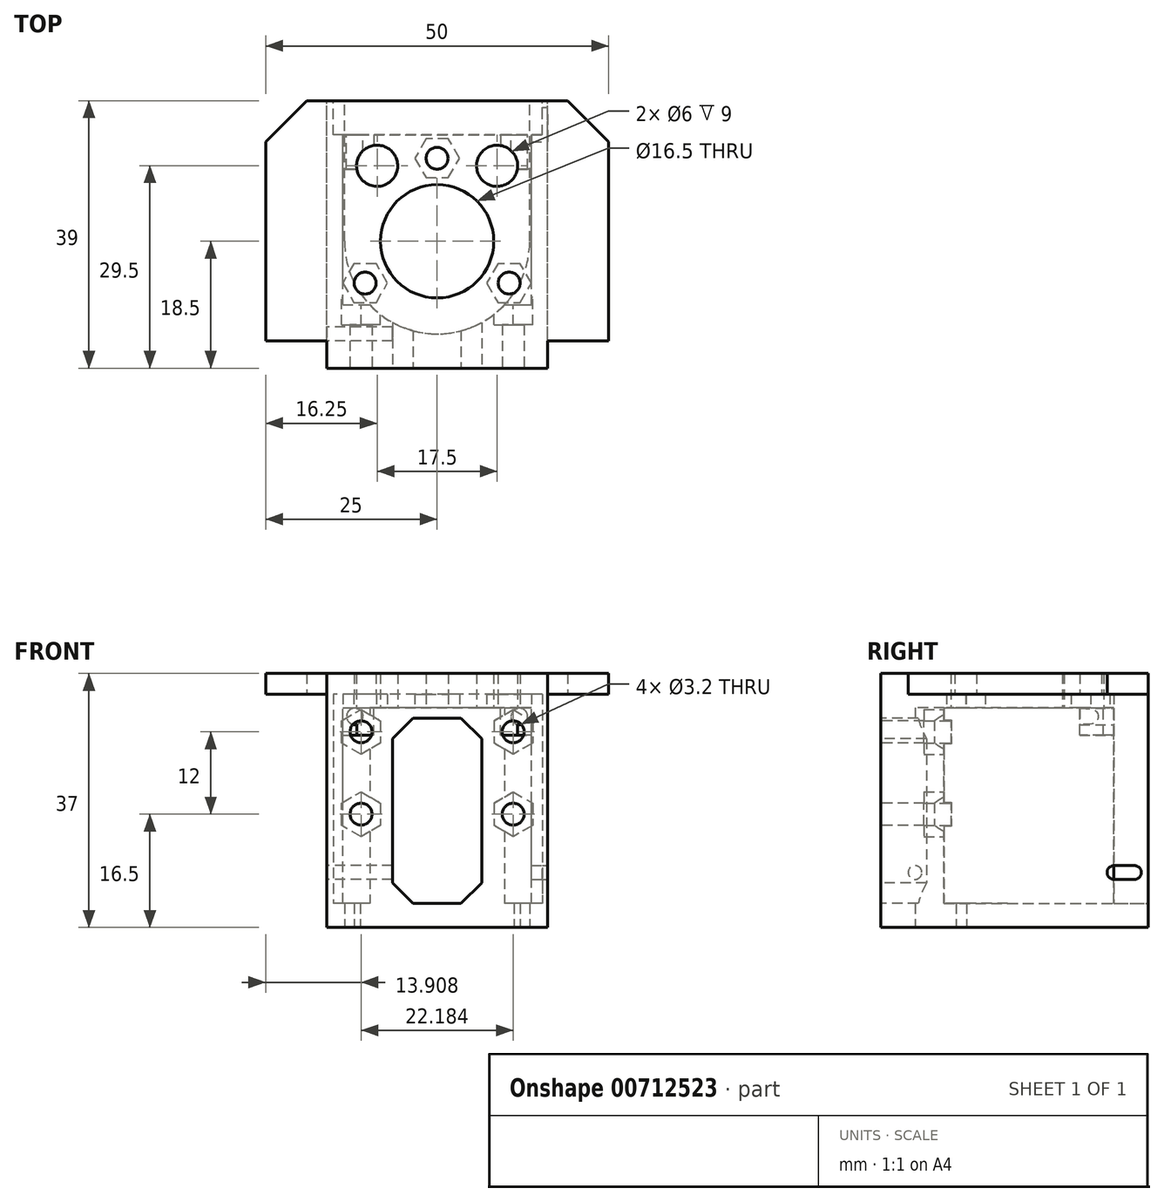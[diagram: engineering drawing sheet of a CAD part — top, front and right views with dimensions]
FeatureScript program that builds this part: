
annotation { "Feature Type Name" : "Feature", "Feature Type Description" : "" }
export const myFeature = defineFeature(function(context is Context, id is Id, definition is map)
    precondition{}
    {
        {
            var Q0;
            Q0=qCreatedBy(makeId("Top.planeOp"),FACE);
            var sketch = newSketch(context, id + "F0", { "sketchPlane" : qUnion([Q0])});
            skLineSegment(sketch, "E0", {"start": v(-25, 0) * mm, "end": v(-25, 29) * mm});
            skLineSegment(sketch, "E1", {"start": v(-25, 29) * mm, "end": v(-19, 35) * mm});
            skLineSegment(sketch, "E2", {"start": v(-19, 35) * mm, "end": v(19, 35) * mm});
            skLineSegment(sketch, "E3", {"start": v(19, 35) * mm, "end": v(25, 29) * mm});
            skLineSegment(sketch, "E4", {"start": v(25, 29) * mm, "end": v(25, 0) * mm});
            skLineSegment(sketch, "E5", {"start": v(25, 0) * mm, "end": v(16.1, 0) * mm});
            skLineSegment(sketch, "E6", {"start": v(16.1, 0) * mm, "end": v(16.1, -4) * mm});
            skLineSegment(sketch, "E7", {"start": v(16.1, -4) * mm, "end": v(-16.1, -4) * mm});
            skLineSegment(sketch, "E8", {"start": v(-16.1, -4) * mm, "end": v(-16.1, 0) * mm});
            skLineSegment(sketch, "E9", {"start": v(-16.1, 0) * mm, "end": v(-25, 0) * mm});
            skCircle(sketch, "E10", {"center": v(0, 14.5) * mm, "radius": 8.25 * mm});
            skCircle(sketch, "E11", {"center": v(0, 26.6) * mm, "radius": 1.6 * mm});
            skCircle(sketch, "E12", {"center": v(-10.5, 8.4) * mm, "radius": 1.6 * mm});
            skCircle(sketch, "E13", {"center": v(10.5, 8.4) * mm, "radius": 1.6 * mm});
            skCircle(sketch, "E14", {"center": v(-8.75, 25.5) * mm, "radius": 3 * mm});
            skCircle(sketch, "E15", {"center": v(8.75, 25.5) * mm, "radius": 3 * mm});
            skSolve(sketch);
        }
        {
            var Q0;
            Q0=makeQuery(id+"F0.imprint","IMPRINT",FACE,{"disambiguationData":[TD([[makeQuery(id+"F0.imprint","IMPRINT",EDGE,{"derivedFrom":sQuery(id+"F0.wireOp",EDGE,"E0")}),-1.0]])]});
            extrude(context, id + "F1", {"entities" : qUnion([Q0]), "depth" : 3 * mm, "offsetDistance" : 25 * mm});
        }
        {
            var Q0;
            Q0=makeQuery(id+"F1.opExtrude","CAP_FACE",FACE,{"disambiguationData":[OSD([sQuery(id+"F0.wireOp",EDGE,"E0"),sQuery(id+"F0.wireOp",EDGE,"E1"),sQuery(id+"F0.wireOp",EDGE,"E2"),sQuery(id+"F0.wireOp",EDGE,"E3"),sQuery(id+"F0.wireOp",EDGE,"E4"),sQuery(id+"F0.wireOp",EDGE,"E5"),sQuery(id+"F0.wireOp",EDGE,"E6"),sQuery(id+"F0.wireOp",EDGE,"E7"),sQuery(id+"F0.wireOp",EDGE,"E8"),sQuery(id+"F0.wireOp",EDGE,"E9"),sQuery(id+"F0.wireOp",EDGE,"E10"),sQuery(id+"F0.wireOp",EDGE,"E11"),sQuery(id+"F0.wireOp",EDGE,"E12"),sQuery(id+"F0.wireOp",EDGE,"E13"),sQuery(id+"F0.wireOp",EDGE,"E14"),sQuery(id+"F0.wireOp",EDGE,"E15")])],"isStart":true});
            var sketch = newSketch(context, id + "F2", { "sketchPlane" : qUnion([Q0])});
            skLineSegment(sketch, "E16.bottom", {"start": v(-16.1, 4) * mm, "end": v(16.1, 4) * mm});
            skLineSegment(sketch, "E16.top", {"start": v(-16.1, -35) * mm, "end": v(16.1, -35) * mm});
            skLineSegment(sketch, "E16.left", {"start": v(-16.1, 4) * mm, "end": v(-16.1, -35) * mm});
            skLineSegment(sketch, "E16.right", {"start": v(16.1, 4) * mm, "end": v(16.1, -35) * mm});
            skSolve(sketch);
        }
        {
            var Q0;
            {var subQ4=sQuery(id+"F2.wireOp",EDGE,"E16.bottom");Q0=makeQuery(id+"F2.imprint","IMPRINT",FACE,{"disambiguationData":[TD([[makeQuery(id+"F2.imprint","IMPRINT",EDGE,{"derivedFrom":subQ4}),1.0]])]});}
            extrude(context, id + "F3", {"entities" : qUnion([Q0]), "operationType" : NewBodyOperationType.ADD, "depth" : 34 * mm, "offsetDistance" : 25 * mm});
        }
        {
            var Q0;
            Q0=makeQuery(id+"F3.boolean.opBoolean","MERGE",FACE,{"derivedFrom":[makeQuery(id+"F1.opExtrude","SWEPT_FACE",FACE,{"disambiguationData":[OSD([sQuery(id+"F0.wireOp",EDGE,"E2")])]}),makeQuery(id+"F3.opExtrude","SWEPT_FACE",FACE,{"disambiguationData":[OSD([sQuery(id+"F2.wireOp",EDGE,"E16.top")])]})]});
            var sketch = newSketch(context, id + "F4", { "sketchPlane" : qUnion([Q0])});
            skLineSegment(sketch, "E17.bottom", {"start": v(-15.34, 0) * mm, "end": v(15.16, 0) * mm});
            skLineSegment(sketch, "E17.top", {"start": v(-15.34, -30.5) * mm, "end": v(15.16, -30.5) * mm});
            skLineSegment(sketch, "E17.left", {"start": v(-15.34, 0) * mm, "end": v(-15.34, -30.5) * mm});
            skLineSegment(sketch, "E17.right", {"start": v(15.16, 0) * mm, "end": v(15.16, -30.5) * mm});
            skSolve(sketch);
        }
        {
            var Q0;
            Q0=makeQuery(id+"F4.imprint","IMPRINT",FACE,{"disambiguationData":[TD([[makeQuery(id+"F4.imprint","IMPRINT",EDGE,{"derivedFrom":sQuery(id+"F4.wireOp",EDGE,"E17.bottom")}),-1.0]])]});
            extrude(context, id + "F5", {"entities" : qUnion([Q0]), "operationType" : NewBodyOperationType.REMOVE, "oppositeDirection" : true, "depth" : 5 * mm, "offsetDistance" : 25 * mm});
        }
        {
            var Q0;
            Q0=makeQuery(id+"F5.boolean.opBoolean","COPY",FACE,{"derivedFrom":makeQuery(id+"F5.opExtrude","CAP_FACE",FACE,{"disambiguationData":[OSD([sQuery(id+"F4.wireOp",EDGE,"E17.bottom"),sQuery(id+"F4.wireOp",EDGE,"E17.top"),sQuery(id+"F4.wireOp",EDGE,"E17.left"),sQuery(id+"F4.wireOp",EDGE,"E17.right")])],"isStart":false})});
            var sketch = newSketch(context, id + "F6", { "sketchPlane" : qUnion([Q0])});
            skLineSegment(sketch, "E18.bottom", {"start": v(13.75, -30.5) * mm, "end": v(-13.75, -30.5) * mm});
            skLineSegment(sketch, "E18.top", {"start": v(13.75, -2) * mm, "end": v(-13.75, -2) * mm});
            skLineSegment(sketch, "E18.left", {"start": v(13.75, -30.5) * mm, "end": v(13.75, -2) * mm});
            skLineSegment(sketch, "E18.right", {"start": v(-13.75, -30.5) * mm, "end": v(-13.75, -2) * mm});
            skPoint(sketch, "E18.middle", {"position": v(0, -16.25) * mm});
            skSolve(sketch);
        }
        {
            var Q0;
            Q0=makeQuery(id+"F6.imprint","IMPRINT",FACE,{"disambiguationData":[TD([[makeQuery(id+"F6.imprint","IMPRINT",EDGE,{"derivedFrom":sQuery(id+"F6.wireOp",EDGE,"E18.bottom")}),1.0]])]});
            extrude(context, id + "F7", {"entities" : qUnion([Q0]), "operationType" : NewBodyOperationType.REMOVE, "oppositeDirection" : true, "depth" : 24.77 * mm, "offsetDistance" : 25 * mm});
        }
        {
            var Q0;
            Q0=makeQuery(id+"F3.opExtrude","CAP_FACE",FACE,{"disambiguationData":[OSD([sQuery(id+"F0.wireOp",EDGE,"E10"),sQuery(id+"F0.wireOp",EDGE,"E11"),sQuery(id+"F0.wireOp",EDGE,"E12"),sQuery(id+"F0.wireOp",EDGE,"E13"),sQuery(id+"F0.wireOp",EDGE,"E14"),sQuery(id+"F0.wireOp",EDGE,"E15"),sQuery(id+"F2.wireOp",EDGE,"E16.bottom"),sQuery(id+"F2.wireOp",EDGE,"E16.top"),sQuery(id+"F2.wireOp",EDGE,"E16.left"),sQuery(id+"F2.wireOp",EDGE,"E16.right")])],"isStart":false});
            var sketch = newSketch(context, id + "F8", { "sketchPlane" : qUnion([Q0])});
            skCircle(sketch, "E19", {"center": v(0, -14.5) * mm, "radius": 13.5 * mm});
            skLineSegment(sketch, "E20.bottom", {"start": v(13.5, -14.5) * mm, "end": v(-13.5, -14.5) * mm});
            skLineSegment(sketch, "E20.top", {"start": v(13.5, -55.5) * mm, "end": v(-13.5, -55.5) * mm});
            skLineSegment(sketch, "E20.left", {"start": v(13.5, -14.5) * mm, "end": v(13.5, -55.5) * mm});
            skLineSegment(sketch, "E20.right", {"start": v(-13.5, -14.5) * mm, "end": v(-13.5, -55.5) * mm});
            skPoint(sketch, "E20.middle", {"position": v(0, -35) * mm});
            skSolve(sketch);
        }
        {
            var Q0;
            {var subQ2=sQuery(id+"F8.wireOp",EDGE,"E19");var subQ9=makeQuery(id+"F3.opExtrude","CAP_EDGE",EDGE,{"disambiguationData":[OSD([sQuery(id+"F0.wireOp",EDGE,"E14")])],"isStart":false});var subQ10=makeQuery(id+"F8.imprint","INTERSECT",VERTEX,{"disambiguationData":[OD(1.0)],"derivedFrom":[subQ9,subQ2]});Q0=makeQuery(id+"F8.imprint","IMPRINT",FACE,{"disambiguationData":[TD([[makeQuery(id+"F8.imprint","IMPRINT",EDGE,{"disambiguationData":[TD([[subQ10,-1.0]])],"derivedFrom":subQ2}),-1.0]])]});}
            var Q1;
            {var subQ1=sQuery(id+"F8.wireOp",EDGE,"E19");var subQ8=makeQuery(id+"F3.opExtrude","CAP_EDGE",EDGE,{"disambiguationData":[OSD([sQuery(id+"F0.wireOp",EDGE,"E14")])],"isStart":false});var subQ9=makeQuery(id+"F8.imprint","INTERSECT",VERTEX,{"disambiguationData":[OD(1.0)],"derivedFrom":[subQ8,subQ1]});Q1=makeQuery(id+"F8.imprint","IMPRINT",FACE,{"disambiguationData":[TD([[makeQuery(id+"F8.imprint","IMPRINT",EDGE,{"disambiguationData":[TD([[subQ9,-1.0]])],"derivedFrom":subQ1}),1.0]])]});}
            var Q2;
            {var subQ1=sQuery(id+"F8.wireOp",EDGE,"E19");var subQ9=makeQuery(id+"F3.opExtrude","CAP_EDGE",EDGE,{"disambiguationData":[OSD([sQuery(id+"F0.wireOp",EDGE,"E13")])],"isStart":false});var subQ10=makeQuery(id+"F8.imprint","INTERSECT",VERTEX,{"disambiguationData":[OD(1.0)],"derivedFrom":[subQ9,subQ1]});Q2=makeQuery(id+"F8.imprint","IMPRINT",FACE,{"disambiguationData":[TD([[makeQuery(id+"F8.imprint","IMPRINT",EDGE,{"disambiguationData":[TD([[subQ10,-1.0]])],"derivedFrom":subQ1}),1.0]])]});}
            extrude(context, id + "F9", {"entities" : qUnion([Q0, Q1, Q2]), "operationType" : NewBodyOperationType.REMOVE, "oppositeDirection" : true, "depth" : 32 * mm, "offsetDistance" : 25 * mm});
        }
        {
            var Q0;
            Q0=makeQuery(id+"F3.boolean.opBoolean","MERGE",FACE,{"derivedFrom":[makeQuery(id+"F1.opExtrude","SWEPT_FACE",FACE,{"disambiguationData":[OSD([sQuery(id+"F0.wireOp",EDGE,"E7")])]}),makeQuery(id+"F3.opExtrude","SWEPT_FACE",FACE,{"disambiguationData":[OSD([sQuery(id+"F2.wireOp",EDGE,"E16.bottom")])]})]});
            var sketch = newSketch(context, id + "F10", { "sketchPlane" : qUnion([Q0])});
            skLineSegment(sketch, "E21", {"start": v(-6.5, -6.5) * mm, "end": v(-6.5, -27.5) * mm});
            skLineSegment(sketch, "E22", {"start": v(-6.5, -27.5) * mm, "end": v(-3.5, -30.5) * mm});
            skLineSegment(sketch, "E23", {"start": v(-3.5, -30.5) * mm, "end": v(3.5, -30.5) * mm});
            skLineSegment(sketch, "E24", {"start": v(3.5, -30.5) * mm, "end": v(6.5, -27.5) * mm});
            skLineSegment(sketch, "E25", {"start": v(6.5, -27.5) * mm, "end": v(6.5, -6.5) * mm});
            skLineSegment(sketch, "E26", {"start": v(6.5, -6.5) * mm, "end": v(3.5, -3.5) * mm});
            skLineSegment(sketch, "E27", {"start": v(3.5, -3.5) * mm, "end": v(-3.5, -3.5) * mm});
            skLineSegment(sketch, "E28", {"start": v(-3.5, -3.5) * mm, "end": v(-6.5, -6.5) * mm});
            skCircle(sketch, "E29", {"center": v(-11.1, -5.5) * mm, "radius": 1.6 * mm});
            skCircle(sketch, "E30", {"center": v(-11.1, -17.5) * mm, "radius": 1.6 * mm});
            skCircle(sketch, "E31", {"center": v(11.1, -5.5) * mm, "radius": 1.6 * mm});
            skCircle(sketch, "E32", {"center": v(11.1, -17.5) * mm, "radius": 1.6 * mm});
            skSolve(sketch);
        }
        {
            var Q0;
            Q0=makeQuery(id+"F10.imprint","IMPRINT",FACE,{"disambiguationData":[TD([[makeQuery(id+"F10.imprint","IMPRINT",EDGE,{"derivedFrom":sQuery(id+"F10.wireOp",EDGE,"E29")}),1.0]])]});
            var Q1;
            Q1=makeQuery(id+"F10.imprint","IMPRINT",FACE,{"disambiguationData":[TD([[makeQuery(id+"F10.imprint","IMPRINT",EDGE,{"derivedFrom":sQuery(id+"F10.wireOp",EDGE,"E21")}),1.0]])]});
            var Q2;
            Q2=makeQuery(id+"F10.imprint","IMPRINT",FACE,{"disambiguationData":[TD([[makeQuery(id+"F10.imprint","IMPRINT",EDGE,{"derivedFrom":sQuery(id+"F10.wireOp",EDGE,"E30")}),1.0]])]});
            var Q3;
            Q3=makeQuery(id+"F10.imprint","IMPRINT",FACE,{"disambiguationData":[TD([[makeQuery(id+"F10.imprint","IMPRINT",EDGE,{"derivedFrom":sQuery(id+"F10.wireOp",EDGE,"E32")}),1.0]])]});
            var Q4;
            Q4=makeQuery(id+"F10.imprint","IMPRINT",FACE,{"disambiguationData":[TD([[makeQuery(id+"F10.imprint","IMPRINT",EDGE,{"derivedFrom":sQuery(id+"F10.wireOp",EDGE,"E31")}),1.0]])]});
            extrude(context, id + "F11", {"entities" : qUnion([Q0, Q1, Q2, Q3, Q4]), "operationType" : NewBodyOperationType.REMOVE, "endBound" : BoundingType.THROUGH_ALL, "oppositeDirection" : true, "depth" : 25 * mm, "offsetDistance" : 25 * mm});
        }
        {
            var Q0;
            Q0=makeQuery(id+"F9.boolean.opBoolean","MERGE",FACE,{"derivedFrom":[makeQuery(id+"F7.boolean.opBoolean","COPY",FACE,{"derivedFrom":makeQuery(id+"F7.opExtrude","SWEPT_FACE",FACE,{"disambiguationData":[OSD([sQuery(id+"F6.wireOp",EDGE,"E18.top")])]})}),makeQuery(id+"F9.opExtrude","CAP_FACE",FACE,{"disambiguationData":[OSD([sQuery(id+"F0.wireOp",EDGE,"E10"),sQuery(id+"F0.wireOp",EDGE,"E11"),sQuery(id+"F0.wireOp",EDGE,"E12"),sQuery(id+"F0.wireOp",EDGE,"E13"),sQuery(id+"F0.wireOp",EDGE,"E14"),sQuery(id+"F0.wireOp",EDGE,"E15"),sQuery(id+"F2.wireOp",EDGE,"E16.top"),sQuery(id+"F8.wireOp",EDGE,"E19"),sQuery(id+"F8.wireOp",EDGE,"E20.left"),sQuery(id+"F8.wireOp",EDGE,"E20.right")])],"isStart":false})]});
            var sketch = newSketch(context, id + "F12", { "sketchPlane" : qUnion([Q0])});
            skCircle(sketch, "E33.cCircle", {"center": v(0, -26.6) * mm, "radius": 2.83 * mm, "construction": true});
            skLineSegment(sketch, "E33.0", {"start": v(3.26, -26.6) * mm, "end": v(1.63, -29.43) * mm});
            skLineSegment(sketch, "E33.1", {"start": v(1.63, -29.42) * mm, "end": v(-1.63, -29.42) * mm});
            skLineSegment(sketch, "E33.2", {"start": v(-1.63, -29.42) * mm, "end": v(-3.26, -26.6) * mm});
            skLineSegment(sketch, "E33.3", {"start": v(-3.26, -26.6) * mm, "end": v(-1.63, -23.77) * mm});
            skLineSegment(sketch, "E33.4", {"start": v(-1.63, -23.77) * mm, "end": v(1.63, -23.77) * mm});
            skLineSegment(sketch, "E33.5", {"start": v(1.63, -23.78) * mm, "end": v(3.26, -26.6) * mm});
            skPoint(sketch, "E33.0.midPoint", {"position": v(2.45, -28.01) * mm});
            skCircle(sketch, "E34.cCircle", {"center": v(-10.5, -8.4) * mm, "radius": 2.83 * mm, "construction": true});
            skLineSegment(sketch, "E34.0", {"start": v(-7.24, -8.4) * mm, "end": v(-8.87, -11.23) * mm});
            skLineSegment(sketch, "E34.1", {"start": v(-8.87, -11.23) * mm, "end": v(-12.13, -11.23) * mm});
            skLineSegment(sketch, "E34.2", {"start": v(-12.13, -11.22) * mm, "end": v(-13.76, -8.4) * mm});
            skLineSegment(sketch, "E34.3", {"start": v(-13.76, -8.4) * mm, "end": v(-12.13, -5.58) * mm});
            skLineSegment(sketch, "E34.4", {"start": v(-12.13, -5.58) * mm, "end": v(-8.87, -5.58) * mm});
            skLineSegment(sketch, "E34.5", {"start": v(-8.87, -5.57) * mm, "end": v(-7.24, -8.4) * mm});
            skPoint(sketch, "E34.0.midPoint", {"position": v(-8.05, -9.81) * mm});
            skCircle(sketch, "E35.cCircle", {"center": v(10.5, -8.4) * mm, "radius": 2.83 * mm, "construction": true});
            skLineSegment(sketch, "E35.0", {"start": v(13.76, -8.4) * mm, "end": v(12.13, -11.22) * mm});
            skLineSegment(sketch, "E35.1", {"start": v(12.13, -11.22) * mm, "end": v(8.87, -11.22) * mm});
            skLineSegment(sketch, "E35.2", {"start": v(8.87, -11.23) * mm, "end": v(7.24, -8.4) * mm});
            skLineSegment(sketch, "E35.3", {"start": v(7.24, -8.4) * mm, "end": v(8.87, -5.58) * mm});
            skLineSegment(sketch, "E35.4", {"start": v(8.87, -5.58) * mm, "end": v(12.13, -5.58) * mm});
            skLineSegment(sketch, "E35.5", {"start": v(12.13, -5.58) * mm, "end": v(13.76, -8.4) * mm});
            skPoint(sketch, "E35.0.midPoint", {"position": v(12.95, -9.81) * mm});
            skSolve(sketch);
        }
        {
            var Q0;
            Q0=makeQuery(id+"F12.imprint","IMPRINT",FACE,{"disambiguationData":[TD([[makeQuery(id+"F12.imprint","IMPRINT",EDGE,{"derivedFrom":sQuery(id+"F12.wireOp",EDGE,"E34.0")}),-1.0]])]});
            var Q1;
            {var subQ2=sQuery(id+"F12.wireOp",EDGE,"E35.1");Q1=makeQuery(id+"F12.imprint","IMPRINT",FACE,{"disambiguationData":[TD([[makeQuery(id+"F12.imprint","IMPRINT",EDGE,{"derivedFrom":subQ2}),-1.0]])]});}
            var Q2;
            Q2=makeQuery(id+"F12.imprint","IMPRINT",FACE,{"disambiguationData":[TD([[makeQuery(id+"F12.imprint","IMPRINT",EDGE,{"derivedFrom":sQuery(id+"F12.wireOp",EDGE,"E33.0")}),-1.0]])]});
            extrude(context, id + "F13", {"entities" : qUnion([Q0, Q1, Q2]), "operationType" : NewBodyOperationType.REMOVE, "oppositeDirection" : true, "depth" : 2 * mm, "offsetDistance" : 25 * mm});
        }
        {
            var Q0;
            Q0=makeQuery(id+"F9.boolean.opBoolean","MERGE",FACE,{"derivedFrom":[makeQuery(id+"F7.boolean.opBoolean","COPY",FACE,{"derivedFrom":makeQuery(id+"F7.opExtrude","SWEPT_FACE",FACE,{"disambiguationData":[OSD([sQuery(id+"F6.wireOp",EDGE,"E18.top")])]})}),makeQuery(id+"F9.opExtrude","CAP_FACE",FACE,{"disambiguationData":[OSD([sQuery(id+"F0.wireOp",EDGE,"E10"),sQuery(id+"F0.wireOp",EDGE,"E11"),sQuery(id+"F0.wireOp",EDGE,"E12"),sQuery(id+"F0.wireOp",EDGE,"E13"),sQuery(id+"F0.wireOp",EDGE,"E14"),sQuery(id+"F0.wireOp",EDGE,"E15"),sQuery(id+"F2.wireOp",EDGE,"E16.top"),sQuery(id+"F8.wireOp",EDGE,"E19"),sQuery(id+"F8.wireOp",EDGE,"E20.left"),sQuery(id+"F8.wireOp",EDGE,"E20.right")])],"isStart":false})]});
            var sketch = newSketch(context, id + "F14", { "sketchPlane" : qUnion([Q0])});
            skLineSegment(sketch, "E36.bottom", {"start": v(13.75, -30) * mm, "end": v(9.25, -30) * mm});
            skLineSegment(sketch, "E36.top", {"start": v(13.75, -25) * mm, "end": v(9.25, -25) * mm});
            skLineSegment(sketch, "E36.left", {"start": v(13.75, -30) * mm, "end": v(13.75, -25) * mm});
            skLineSegment(sketch, "E36.right", {"start": v(9.25, -30) * mm, "end": v(9.25, -25) * mm});
            skLineSegment(sketch, "E37.bottom", {"start": v(-13.75, -30) * mm, "end": v(-9.25, -30) * mm});
            skLineSegment(sketch, "E37.top", {"start": v(-13.75, -25) * mm, "end": v(-9.25, -25) * mm});
            skLineSegment(sketch, "E37.left", {"start": v(-13.75, -30) * mm, "end": v(-13.75, -25) * mm});
            skLineSegment(sketch, "E37.right", {"start": v(-9.25, -30) * mm, "end": v(-9.25, -25) * mm});
            skSolve(sketch);
        }
        {
            var Q0;
            {var subQ1=sQuery(id+"F14.wireOp",EDGE,"E37.bottom");Q0=makeQuery(id+"F14.imprint","IMPRINT",FACE,{"disambiguationData":[TD([[makeQuery(id+"F14.imprint","IMPRINT",EDGE,{"derivedFrom":subQ1}),1.0]])]});}
            var Q1;
            {var subQ1=sQuery(id+"F14.wireOp",EDGE,"E36.bottom");Q1=makeQuery(id+"F14.imprint","IMPRINT",FACE,{"disambiguationData":[TD([[makeQuery(id+"F14.imprint","IMPRINT",EDGE,{"derivedFrom":subQ1}),1.0]])]});}
            extrude(context, id + "F15", {"entities" : qUnion([Q0, Q1]), "operationType" : NewBodyOperationType.ADD, "depth" : 4 * mm, "offsetDistance" : 25 * mm});
        }
        {
            var Q0;
            Q0=makeQuery(id+"F3.boolean.opBoolean","MERGE",FACE,{"derivedFrom":[makeQuery(id+"F1.opExtrude","SWEPT_FACE",FACE,{"disambiguationData":[OSD([sQuery(id+"F0.wireOp",EDGE,"E7")])]}),makeQuery(id+"F3.opExtrude","SWEPT_FACE",FACE,{"disambiguationData":[OSD([sQuery(id+"F2.wireOp",EDGE,"E16.bottom")])]})]});
            var sketch = newSketch(context, id + "F16", { "sketchPlane" : qUnion([Q0])});
            skCircle(sketch, "E38.cCircle", {"center": v(-11.1, -5.5) * mm, "radius": 2.83 * mm, "construction": true});
            skLineSegment(sketch, "E38.0", {"start": v(-8.27, -7.13) * mm, "end": v(-11.1, -8.76) * mm});
            skLineSegment(sketch, "E38.1", {"start": v(-11.1, -8.76) * mm, "end": v(-13.92, -7.13) * mm});
            skLineSegment(sketch, "E38.2", {"start": v(-13.92, -7.13) * mm, "end": v(-13.92, -3.87) * mm});
            skLineSegment(sketch, "E38.3", {"start": v(-13.92, -3.87) * mm, "end": v(-11.1, -2.24) * mm});
            skLineSegment(sketch, "E38.4", {"start": v(-11.1, -2.24) * mm, "end": v(-8.27, -3.87) * mm});
            skLineSegment(sketch, "E38.5", {"start": v(-8.27, -3.87) * mm, "end": v(-8.27, -7.13) * mm});
            skPoint(sketch, "E38.0.midPoint", {"position": v(-9.68, -7.95) * mm});
            skCircle(sketch, "E39.cCircle", {"center": v(-11.1, -17.5) * mm, "radius": 2.83 * mm, "construction": true});
            skLineSegment(sketch, "E39.0", {"start": v(-8.27, -19.13) * mm, "end": v(-11.1, -20.76) * mm});
            skLineSegment(sketch, "E39.1", {"start": v(-11.1, -20.76) * mm, "end": v(-13.92, -19.13) * mm});
            skLineSegment(sketch, "E39.2", {"start": v(-13.92, -19.13) * mm, "end": v(-13.92, -15.87) * mm});
            skLineSegment(sketch, "E39.3", {"start": v(-13.92, -15.87) * mm, "end": v(-11.1, -14.24) * mm});
            skLineSegment(sketch, "E39.4", {"start": v(-11.1, -14.24) * mm, "end": v(-8.27, -15.87) * mm});
            skLineSegment(sketch, "E39.5", {"start": v(-8.27, -15.87) * mm, "end": v(-8.27, -19.13) * mm});
            skPoint(sketch, "E39.0.midPoint", {"position": v(-9.68, -19.95) * mm});
            skCircle(sketch, "E40.cCircle", {"center": v(11.1, -5.5) * mm, "radius": 2.83 * mm, "construction": true});
            skLineSegment(sketch, "E40.0", {"start": v(13.92, -7.13) * mm, "end": v(11.1, -8.76) * mm});
            skLineSegment(sketch, "E40.1", {"start": v(11.1, -8.76) * mm, "end": v(8.27, -7.13) * mm});
            skLineSegment(sketch, "E40.2", {"start": v(8.27, -7.13) * mm, "end": v(8.27, -3.87) * mm});
            skLineSegment(sketch, "E40.3", {"start": v(8.27, -3.87) * mm, "end": v(11.1, -2.24) * mm});
            skLineSegment(sketch, "E40.4", {"start": v(11.1, -2.24) * mm, "end": v(13.92, -3.87) * mm});
            skLineSegment(sketch, "E40.5", {"start": v(13.92, -3.87) * mm, "end": v(13.92, -7.13) * mm});
            skPoint(sketch, "E40.0.midPoint", {"position": v(12.5, -7.95) * mm});
            skCircle(sketch, "E41.cCircle", {"center": v(11.1, -17.5) * mm, "radius": 2.82 * mm, "construction": true});
            skLineSegment(sketch, "E41.0", {"start": v(13.92, -19.13) * mm, "end": v(11.1, -20.76) * mm});
            skLineSegment(sketch, "E41.1", {"start": v(11.1, -20.76) * mm, "end": v(8.27, -19.13) * mm});
            skLineSegment(sketch, "E41.2", {"start": v(8.27, -19.13) * mm, "end": v(8.27, -15.87) * mm});
            skLineSegment(sketch, "E41.3", {"start": v(8.27, -15.87) * mm, "end": v(11.1, -14.24) * mm});
            skLineSegment(sketch, "E41.4", {"start": v(11.1, -14.24) * mm, "end": v(13.92, -15.87) * mm});
            skLineSegment(sketch, "E41.5", {"start": v(13.92, -15.87) * mm, "end": v(13.92, -19.13) * mm});
            skPoint(sketch, "E41.0.midPoint", {"position": v(12.5, -19.95) * mm});
            skSolve(sketch);
        }
        {
            var Q0;
            Q0=makeQuery(id+"F16.imprint","IMPRINT",FACE,{"disambiguationData":[TD([[makeQuery(id+"F16.imprint","IMPRINT",EDGE,{"derivedFrom":sQuery(id+"F16.wireOp",EDGE,"E38.0")}),-1.0]])]});
            var Q1;
            Q1=makeQuery(id+"F16.imprint","IMPRINT",FACE,{"disambiguationData":[TD([[makeQuery(id+"F16.imprint","IMPRINT",EDGE,{"derivedFrom":sQuery(id+"F16.wireOp",EDGE,"E39.0")}),-1.0]])]});
            var Q2;
            Q2=makeQuery(id+"F16.imprint","IMPRINT",FACE,{"disambiguationData":[TD([[makeQuery(id+"F16.imprint","IMPRINT",EDGE,{"derivedFrom":sQuery(id+"F16.wireOp",EDGE,"E41.0")}),-1.0]])]});
            var Q3;
            Q3=makeQuery(id+"F16.imprint","IMPRINT",FACE,{"disambiguationData":[TD([[makeQuery(id+"F16.imprint","IMPRINT",EDGE,{"derivedFrom":sQuery(id+"F16.wireOp",EDGE,"E40.0")}),-1.0]])]});
            extrude(context, id + "F17", {"entities" : qUnion([Q0, Q1, Q2, Q3]), "depth" : 4 * mm, "offsetDistance" : 25 * mm});
        }
        {
            var Q0;
            Q0=makeQuery(id+"F17.opExtrude","SWEPT_BODY",BODY,{"disambiguationData":[OSD([sQuery(id+"F10.wireOp",EDGE,"E29"),sQuery(id+"F16.wireOp",EDGE,"E38.0"),sQuery(id+"F16.wireOp",EDGE,"E38.1"),sQuery(id+"F16.wireOp",EDGE,"E38.2"),sQuery(id+"F16.wireOp",EDGE,"E38.3"),sQuery(id+"F16.wireOp",EDGE,"E38.4"),sQuery(id+"F16.wireOp",EDGE,"E38.5")])]});
            var Q1;
            Q1=makeQuery(id+"F17.opExtrude","SWEPT_BODY",BODY,{"disambiguationData":[OSD([sQuery(id+"F10.wireOp",EDGE,"E30"),sQuery(id+"F16.wireOp",EDGE,"E39.0"),sQuery(id+"F16.wireOp",EDGE,"E39.1"),sQuery(id+"F16.wireOp",EDGE,"E39.2"),sQuery(id+"F16.wireOp",EDGE,"E39.3"),sQuery(id+"F16.wireOp",EDGE,"E39.4"),sQuery(id+"F16.wireOp",EDGE,"E39.5")])]});
            var Q2;
            Q2=makeQuery(id+"F17.opExtrude","SWEPT_BODY",BODY,{"disambiguationData":[OSD([sQuery(id+"F10.wireOp",EDGE,"E31"),sQuery(id+"F16.wireOp",EDGE,"E40.0"),sQuery(id+"F16.wireOp",EDGE,"E40.1"),sQuery(id+"F16.wireOp",EDGE,"E40.2"),sQuery(id+"F16.wireOp",EDGE,"E40.3"),sQuery(id+"F16.wireOp",EDGE,"E40.4"),sQuery(id+"F16.wireOp",EDGE,"E40.5")])]});
            var Q3;
            Q3=makeQuery(id+"F17.opExtrude","SWEPT_BODY",BODY,{"disambiguationData":[OSD([sQuery(id+"F10.wireOp",EDGE,"E32"),sQuery(id+"F16.wireOp",EDGE,"E41.0"),sQuery(id+"F16.wireOp",EDGE,"E41.1"),sQuery(id+"F16.wireOp",EDGE,"E41.2"),sQuery(id+"F16.wireOp",EDGE,"E41.3"),sQuery(id+"F16.wireOp",EDGE,"E41.4"),sQuery(id+"F16.wireOp",EDGE,"E41.5")])]});
            transform(context, id + "F18", {"entities" : qUnion([Q0, Q1, Q2, Q3]), "transformType" : TransformType.TRANSLATION_3D, "dx" : 0 * mm, "dy" : 10.3 * mm, "dz" : 0 * mm, "makeCopy" : false});
        }
        {
            var Q0;
            Q0=makeQuery(id+"F17.opExtrude","SWEPT_BODY",BODY,{"disambiguationData":[OSD([sQuery(id+"F10.wireOp",EDGE,"E29"),sQuery(id+"F16.wireOp",EDGE,"E38.0"),sQuery(id+"F16.wireOp",EDGE,"E38.1"),sQuery(id+"F16.wireOp",EDGE,"E38.2"),sQuery(id+"F16.wireOp",EDGE,"E38.3"),sQuery(id+"F16.wireOp",EDGE,"E38.4"),sQuery(id+"F16.wireOp",EDGE,"E38.5")])]});
            var Q1;
            Q1=makeQuery(id+"F17.opExtrude","SWEPT_BODY",BODY,{"disambiguationData":[OSD([sQuery(id+"F10.wireOp",EDGE,"E30"),sQuery(id+"F16.wireOp",EDGE,"E39.0"),sQuery(id+"F16.wireOp",EDGE,"E39.1"),sQuery(id+"F16.wireOp",EDGE,"E39.2"),sQuery(id+"F16.wireOp",EDGE,"E39.3"),sQuery(id+"F16.wireOp",EDGE,"E39.4"),sQuery(id+"F16.wireOp",EDGE,"E39.5")])]});
            var Q2;
            Q2=makeQuery(id+"F17.opExtrude","SWEPT_BODY",BODY,{"disambiguationData":[OSD([sQuery(id+"F10.wireOp",EDGE,"E31"),sQuery(id+"F16.wireOp",EDGE,"E40.0"),sQuery(id+"F16.wireOp",EDGE,"E40.1"),sQuery(id+"F16.wireOp",EDGE,"E40.2"),sQuery(id+"F16.wireOp",EDGE,"E40.3"),sQuery(id+"F16.wireOp",EDGE,"E40.4"),sQuery(id+"F16.wireOp",EDGE,"E40.5")])]});
            var Q3;
            Q3=makeQuery(id+"F17.opExtrude","SWEPT_BODY",BODY,{"disambiguationData":[OSD([sQuery(id+"F10.wireOp",EDGE,"E32"),sQuery(id+"F16.wireOp",EDGE,"E41.0"),sQuery(id+"F16.wireOp",EDGE,"E41.1"),sQuery(id+"F16.wireOp",EDGE,"E41.2"),sQuery(id+"F16.wireOp",EDGE,"E41.3"),sQuery(id+"F16.wireOp",EDGE,"E41.4"),sQuery(id+"F16.wireOp",EDGE,"E41.5")])]});
            var Q4;
            Q4=makeQuery(id+"F1.opExtrude","SWEPT_BODY",BODY,{"disambiguationData":[OSD([sQuery(id+"F0.wireOp",EDGE,"E0"),sQuery(id+"F0.wireOp",EDGE,"E1"),sQuery(id+"F0.wireOp",EDGE,"E2"),sQuery(id+"F0.wireOp",EDGE,"E3"),sQuery(id+"F0.wireOp",EDGE,"E4"),sQuery(id+"F0.wireOp",EDGE,"E5"),sQuery(id+"F0.wireOp",EDGE,"E6"),sQuery(id+"F0.wireOp",EDGE,"E7"),sQuery(id+"F0.wireOp",EDGE,"E8"),sQuery(id+"F0.wireOp",EDGE,"E9"),sQuery(id+"F0.wireOp",EDGE,"E10"),sQuery(id+"F0.wireOp",EDGE,"E11"),sQuery(id+"F0.wireOp",EDGE,"E12"),sQuery(id+"F0.wireOp",EDGE,"E13"),sQuery(id+"F0.wireOp",EDGE,"E14"),sQuery(id+"F0.wireOp",EDGE,"E15")])]});
            booleanBodies(context, id + "F19", {"operationType" : BooleanOperationType.SUBTRACTION, "tools" : qUnion([Q0, Q1, Q2, Q3]), "targets" : qUnion([Q4])});
        }
        {
            var Q0;
            Q0=makeQuery(id+"F15.boolean.opBoolean","MERGE",FACE,{"derivedFrom":[makeQuery(id+"F5.boolean.opBoolean","COPY",FACE,{"derivedFrom":makeQuery(id+"F5.opExtrude","CAP_FACE",FACE,{"disambiguationData":[OSD([sQuery(id+"F4.wireOp",EDGE,"E17.bottom"),sQuery(id+"F4.wireOp",EDGE,"E17.top"),sQuery(id+"F4.wireOp",EDGE,"E17.left"),sQuery(id+"F4.wireOp",EDGE,"E17.right")])],"isStart":false})}),makeQuery(id+"F15.opExtrude","SWEPT_FACE",FACE,{"disambiguationData":[OSD([sQuery(id+"F14.wireOp",EDGE,"E36.bottom")])]}),makeQuery(id+"F15.opExtrude","SWEPT_FACE",FACE,{"disambiguationData":[OSD([sQuery(id+"F14.wireOp",EDGE,"E37.bottom")])]})]});
            var sketch = newSketch(context, id + "F20", { "sketchPlane" : qUnion([Q0])});
            skCircle(sketch, "E42", {"center": v(-12, -3.25) * mm, "radius": 1.2 * mm});
            skCircle(sketch, "E43", {"center": v(12, -3.25) * mm, "radius": 1.2 * mm});
            skSolve(sketch);
        }
        {
            var Q0;
            Q0=makeQuery(id+"F20.imprint","IMPRINT",FACE,{"disambiguationData":[TD([[makeQuery(id+"F20.imprint","IMPRINT",EDGE,{"derivedFrom":sQuery(id+"F20.wireOp",EDGE,"E42")}),1.0]])]});
            var Q1;
            Q1=makeQuery(id+"F20.imprint","IMPRINT",FACE,{"disambiguationData":[TD([[makeQuery(id+"F20.imprint","IMPRINT",EDGE,{"derivedFrom":sQuery(id+"F20.wireOp",EDGE,"E43")}),1.0]])]});
            extrude(context, id + "F21", {"entities" : qUnion([Q0, Q1]), "operationType" : NewBodyOperationType.REMOVE, "endBound" : BoundingType.UP_TO_NEXT, "oppositeDirection" : true, "depth" : 25 * mm, "offsetDistance" : 25 * mm});
        }
        {
            var Q0;
            Q0=makeQuery(id+"F3.boolean.opBoolean","MERGE",FACE,{"derivedFrom":[makeQuery(id+"F1.opExtrude","SWEPT_FACE",FACE,{"disambiguationData":[OSD([sQuery(id+"F0.wireOp",EDGE,"E8")])]}),makeQuery(id+"F3.opExtrude","SWEPT_FACE",FACE,{"disambiguationData":[OSD([sQuery(id+"F2.wireOp",EDGE,"E16.left")])]})]});
            var sketch = newSketch(context, id + "F22", { "sketchPlane" : qUnion([Q0])});
            skCircle(sketch, "E44", {"center": v(-1, -26) * mm, "radius": 1 * mm});
            skSolve(sketch);
        }
        {
            var Q0;
            Q0=makeQuery(id+"F22.imprint","IMPRINT",FACE,{"disambiguationData":[TD([[makeQuery(id+"F22.imprint","IMPRINT",EDGE,{"derivedFrom":sQuery(id+"F22.wireOp",EDGE,"E44")}),1.0]])]});
            extrude(context, id + "F23", {"entities" : qUnion([Q0]), "operationType" : NewBodyOperationType.REMOVE, "endBound" : BoundingType.UP_TO_NEXT, "oppositeDirection" : true, "depth" : 25 * mm, "offsetDistance" : 25 * mm});
        }
        {
            var Q0;
            Q0=makeQuery(id+"F3.boolean.opBoolean","MERGE",FACE,{"derivedFrom":[makeQuery(id+"F1.opExtrude","SWEPT_FACE",FACE,{"disambiguationData":[OSD([sQuery(id+"F0.wireOp",EDGE,"E6")])]}),makeQuery(id+"F3.opExtrude","SWEPT_FACE",FACE,{"disambiguationData":[OSD([sQuery(id+"F2.wireOp",EDGE,"E16.right")])]})]});
            var sketch = newSketch(context, id + "F24", { "sketchPlane" : qUnion([Q0])});
            skCircle(sketch, "E45", {"center": v(30, -26) * mm, "radius": 1 * mm});
            skCircle(sketch, "E46", {"center": v(33, -26) * mm, "radius": 1 * mm});
            skLineSegment(sketch, "E47.bottom", {"start": v(33, -27) * mm, "end": v(30, -27) * mm});
            skLineSegment(sketch, "E47.top", {"start": v(33, -25) * mm, "end": v(30, -25) * mm});
            skLineSegment(sketch, "E47.left", {"start": v(33, -27) * mm, "end": v(33, -25) * mm});
            skLineSegment(sketch, "E47.right", {"start": v(30, -27) * mm, "end": v(30, -25) * mm});
            skPoint(sketch, "E47.middle", {"position": v(31.5, -26) * mm});
            skSolve(sketch);
        }
        {
            var Q0;
            {var subQ0=sQuery(id+"F24.wireOp",EDGE,"E47.right");var subQ1=sQuery(id+"F24.wireOp",EDGE,"E45");var subQ2=makeQuery(id+"F24.imprint","INTERSECT",VERTEX,{"disambiguationData":[OD(0.0)],"derivedFrom":[subQ1,subQ0]});Q0=makeQuery(id+"F24.imprint","IMPRINT",FACE,{"disambiguationData":[TD([[makeQuery(id+"F24.imprint","IMPRINT",EDGE,{"disambiguationData":[TD([[subQ2,1.0]])],"derivedFrom":subQ1}),1.0]])]});}
            var Q1;
            {var subQ0=sQuery(id+"F24.wireOp",EDGE,"E47.right");var subQ1=sQuery(id+"F24.wireOp",EDGE,"E45");var subQ2=makeQuery(id+"F24.imprint","INTERSECT",VERTEX,{"disambiguationData":[OD(0.0)],"derivedFrom":[subQ1,subQ0]});Q1=makeQuery(id+"F24.imprint","IMPRINT",FACE,{"disambiguationData":[TD([[makeQuery(id+"F24.imprint","IMPRINT",EDGE,{"disambiguationData":[TD([[subQ2,-1.0]])],"derivedFrom":subQ1}),1.0]])]});}
            var Q2;
            {var subQ1=sQuery(id+"F24.wireOp",EDGE,"E47.bottom");Q2=makeQuery(id+"F24.imprint","IMPRINT",FACE,{"disambiguationData":[TD([[makeQuery(id+"F24.imprint","IMPRINT",EDGE,{"derivedFrom":subQ1}),-1.0]])]});}
            var Q3;
            {var subQ0=sQuery(id+"F24.wireOp",EDGE,"E47.left");var subQ1=sQuery(id+"F24.wireOp",EDGE,"E46");var subQ2=makeQuery(id+"F24.imprint","INTERSECT",VERTEX,{"disambiguationData":[OD(0.0)],"derivedFrom":[subQ1,subQ0]});Q3=makeQuery(id+"F24.imprint","IMPRINT",FACE,{"disambiguationData":[TD([[makeQuery(id+"F24.imprint","IMPRINT",EDGE,{"disambiguationData":[TD([[subQ2,1.0]])],"derivedFrom":subQ1}),1.0]])]});}
            var Q4;
            {var subQ0=sQuery(id+"F24.wireOp",EDGE,"E47.left");var subQ1=sQuery(id+"F24.wireOp",EDGE,"E46");var subQ2=makeQuery(id+"F24.imprint","INTERSECT",VERTEX,{"disambiguationData":[OD(0.0)],"derivedFrom":[subQ1,subQ0]});Q4=makeQuery(id+"F24.imprint","IMPRINT",FACE,{"disambiguationData":[TD([[makeQuery(id+"F24.imprint","IMPRINT",EDGE,{"disambiguationData":[TD([[subQ2,-1.0]])],"derivedFrom":subQ1}),1.0]])]});}
            extrude(context, id + "F25", {"entities" : qUnion([Q0, Q1, Q2, Q3, Q4]), "operationType" : NewBodyOperationType.REMOVE, "endBound" : BoundingType.UP_TO_NEXT, "oppositeDirection" : true, "depth" : 25 * mm, "offsetDistance" : 25 * mm});
        }
    });
